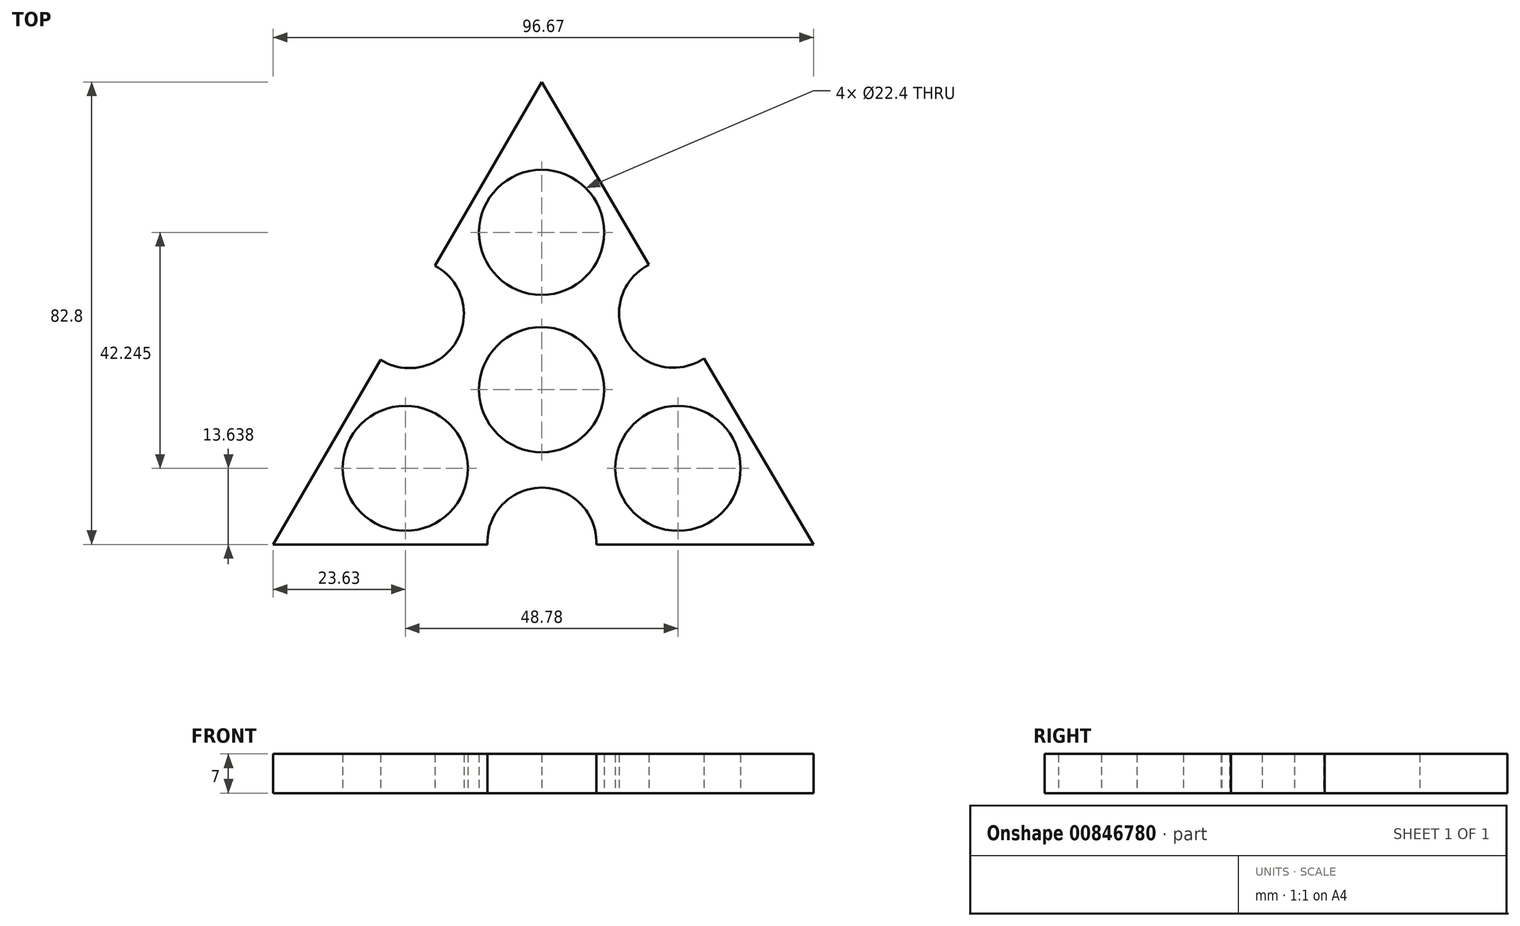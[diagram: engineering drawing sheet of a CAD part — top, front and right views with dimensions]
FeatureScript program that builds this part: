
annotation { "Feature Type Name" : "Feature", "Feature Type Description" : "" }
export const myFeature = defineFeature(function(context is Context, id is Id, definition is map)
    precondition{}
    {
        {
            var Q0;
            Q0=qCreatedBy(makeId("Top.planeOp"),FACE);
            var sketch = newSketch(context, id + "F0", { "sketchPlane" : qUnion([Q0])});
            skCircle(sketch, "E0", {"center": v(0, 0) * mm, "radius": 11.2 * mm});
            skCircle(sketch, "E1", {"center": v(0, 28.16) * mm, "radius": 11.2 * mm});
            skCircle(sketch, "E2.1.0", {"center": v(-24.4, -14.08) * mm, "radius": 11.2 * mm});
            skCircle(sketch, "E2.2.0", {"center": v(24.4, -14.08) * mm, "radius": 11.2 * mm});
            skPoint(sketch, "E3.center.orphan", {"position": v(-23.65, 13.6) * mm});
            skPoint(sketch, "E2.1.1.start.orphan", {"position": v(-35.82, -7.48) * mm});
            skPoint(sketch, "E4.end.orphan", {"position": v(-11.48, 34.69) * mm});
            skLineSegment(sketch, "E5", {"start": v(0, 55.08) * mm, "end": v(-19.07, 22.2) * mm});
            skLineSegment(sketch, "E6", {"start": v(-48.02, -27.72) * mm, "end": v(-9.69, -27.72) * mm});
            skLineSegment(sketch, "E7", {"start": v(48.65, -27.72) * mm, "end": v(29.07, 5.61) * mm});
            skArc(sketch, "E8", {"start": v(-28.84, 5.35) * mm, "mid": v(-15.22, 8.71) * mm, "end": v(-19.07, 22.2) * mm});
            skArc(sketch, "E9.1.0", {"start": v(9.78, -27.72) * mm, "mid": v(0.04, -17.54) * mm, "end": v(-9.69, -27.72) * mm});
            skArc(sketch, "E9.2.0", {"start": v(19.22, 22.38) * mm, "mid": v(15.2, 8.74) * mm, "end": v(29.07, 5.61) * mm});
            skLineSegment(sketch, "E10.trimOffspring", {"start": v(-28.84, 5.35) * mm, "end": v(-48.02, -27.72) * mm});
            skLineSegment(sketch, "E11.trimOffspring", {"start": v(19.22, 22.38) * mm, "end": v(0, 55.08) * mm});
            skLineSegment(sketch, "E12.trimOffspring", {"start": v(9.78, -27.72) * mm, "end": v(48.65, -27.72) * mm});
            skSolve(sketch);
        }
        {
            var Q0;
            Q0=makeQuery(id+"F0.imprint","IMPRINT",FACE,{"disambiguationData":[TD([[makeQuery(id+"F0.imprint","IMPRINT",EDGE,{"derivedFrom":sQuery(id+"F0.wireOp",EDGE,"E0")}),-1.0]])]});
            extrude(context, id + "F1", {"entities" : qUnion([Q0]), "depth" : 7 * mm, "offsetDistance" : 25 * mm});
        }
    });
